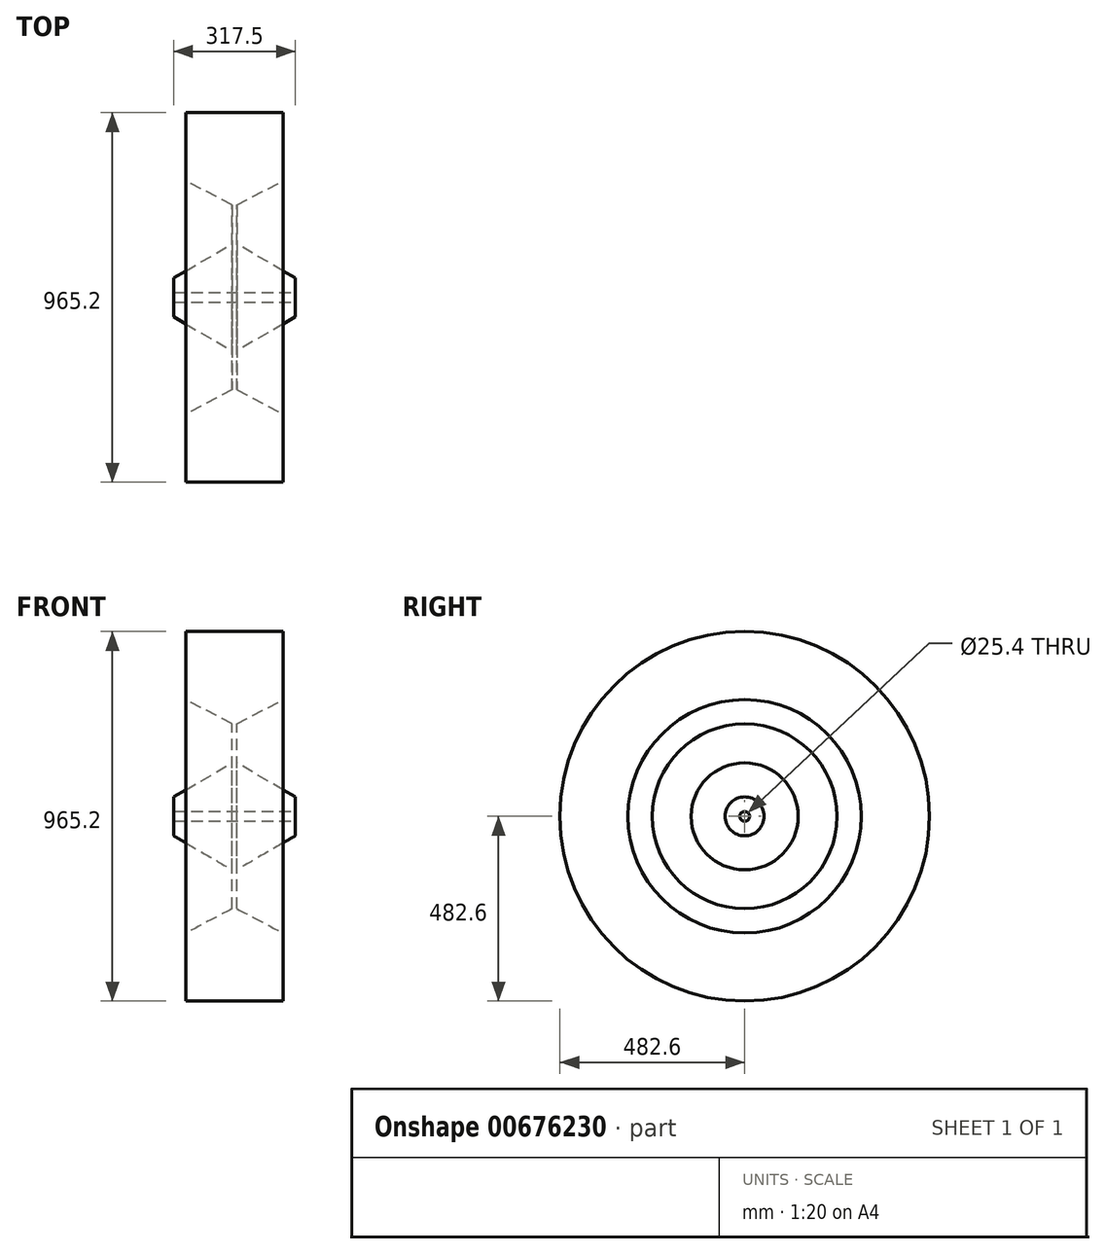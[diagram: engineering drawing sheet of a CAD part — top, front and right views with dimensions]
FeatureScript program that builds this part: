
annotation { "Feature Type Name" : "Feature", "Feature Type Description" : "" }
export const myFeature = defineFeature(function(context is Context, id is Id, definition is map)
    precondition{}
    {
        {
            var Q0;
            Q0=qCreatedBy(makeId("Front.planeOp"),FACE);
            var sketch = newSketch(context, id + "F0", { "sketchPlane" : qUnion([Q0])});
            skLineSegment(sketch, "E0.bottom", {"start": v(0, 0) * mm, "end": v(158.75, 0) * mm, "construction": true});
            skLineSegment(sketch, "E0.top", {"start": v(0, 482.6) * mm, "end": v(158.75, 482.6) * mm, "construction": true});
            skLineSegment(sketch, "E0.left", {"start": v(0, 0) * mm, "end": v(0, 482.6) * mm, "construction": true});
            skLineSegment(sketch, "E0.right", {"start": v(158.75, 0) * mm, "end": v(158.75, 482.6) * mm, "construction": true});
            skLineSegment(sketch, "E1", {"start": v(0, 12.7) * mm, "end": v(158.75, 12.7) * mm});
            skLineSegment(sketch, "E2", {"start": v(158.75, 12.7) * mm, "end": v(158.75, 50.8) * mm});
            skLineSegment(sketch, "E3", {"start": v(158.75, 50.8) * mm, "end": v(6.35, 139.7) * mm});
            skLineSegment(sketch, "E4", {"start": v(6.35, 139.7) * mm, "end": v(6.35, 241.3) * mm});
            skLineSegment(sketch, "E5", {"start": v(6.35, 241.3) * mm, "end": v(127, 304.8) * mm});
            skLineSegment(sketch, "E6", {"start": v(0, 482.6) * mm, "end": v(0, 12.7) * mm});
            skLineSegment(sketch, "E7", {"start": v(0, 482.6) * mm, "end": v(127, 482.6) * mm});
            skLineSegment(sketch, "E8", {"start": v(127, 482.6) * mm, "end": v(127, 304.8) * mm});
            skLineSegment(sketch, "E9.MirrorCS", {"start": v(0, 0) * mm, "end": v(-158.75, 0) * mm, "construction": true});
            skLineSegment(sketch, "E10.MirrorCS", {"start": v(0, 482.6) * mm, "end": v(-127, 482.6) * mm});
            skLineSegment(sketch, "E11.MirrorCS", {"start": v(-127, 482.6) * mm, "end": v(-127, 304.8) * mm});
            skLineSegment(sketch, "E12.MirrorCS", {"start": v(-6.35, 139.7) * mm, "end": v(-6.35, 241.3) * mm});
            skLineSegment(sketch, "E13.MirrorCS", {"start": v(-6.35, 241.3) * mm, "end": v(-127, 304.8) * mm});
            skLineSegment(sketch, "E14.MirrorCS", {"start": v(0, 482.6) * mm, "end": v(-158.75, 482.6) * mm, "construction": true});
            skLineSegment(sketch, "E15.MirrorCS", {"start": v(-158.75, 50.8) * mm, "end": v(-6.35, 139.7) * mm});
            skLineSegment(sketch, "E16.MirrorCS", {"start": v(-158.75, 12.7) * mm, "end": v(-158.75, 50.8) * mm});
            skLineSegment(sketch, "E17.MirrorCS", {"start": v(-158.75, 0) * mm, "end": v(-158.75, 482.6) * mm, "construction": true});
            skLineSegment(sketch, "E18.MirrorCS", {"start": v(0, 12.7) * mm, "end": v(-158.75, 12.7) * mm});
            skSolve(sketch);
        }
        {
            var Q0;
            Q0 = qSketchRegion(id + "F0", true);
            var Q1;
            Q1=sQuery(id+"F0.wireOp",EDGE,"E9.MirrorCS");
            revolve(context, id + "F1", {"entities" : qUnion([Q0]), "axis" : qUnion([Q1]), "revolveType" : RevolveType.FULL});
        }
    });
